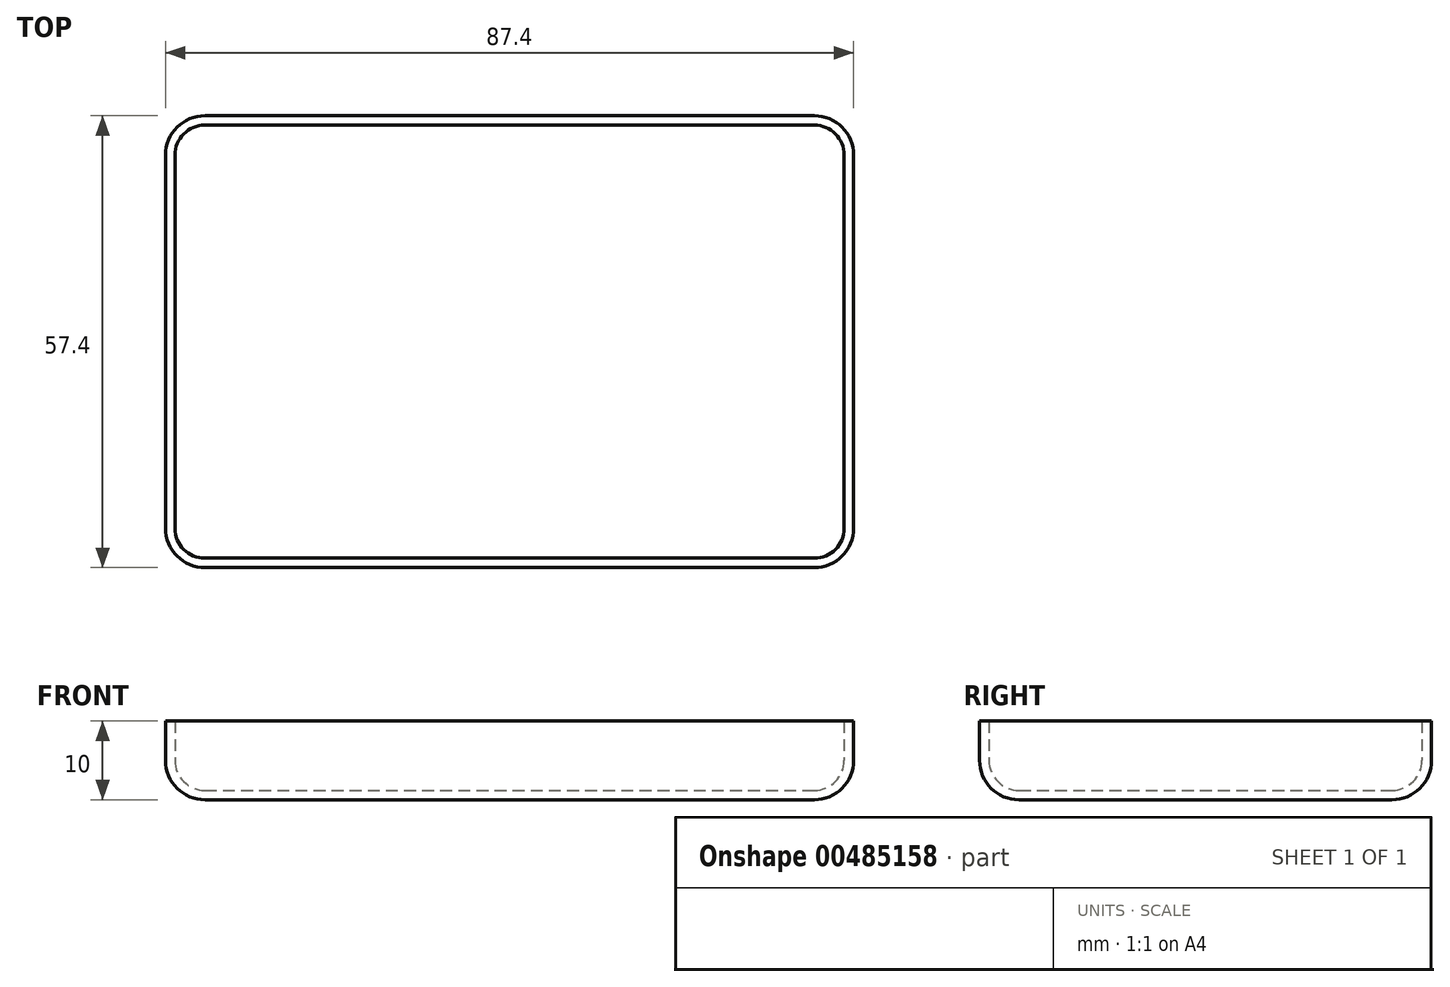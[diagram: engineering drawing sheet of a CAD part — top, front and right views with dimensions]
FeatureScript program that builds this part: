
annotation { "Feature Type Name" : "Feature", "Feature Type Description" : "" }
export const myFeature = defineFeature(function(context is Context, id is Id, definition is map)
    precondition{}
    {
        {
            var Q0;
            Q0=qCreatedBy(makeId("Top.planeOp"),FACE);
            var sketch = newSketch(context, id + "F0", { "sketchPlane" : qUnion([Q0])});
            skLineSegment(sketch, "E0.bottom", {"start": v(42.5, 27.5) * mm, "end": v(-42.5, 27.5) * mm, "construction": true});
            skLineSegment(sketch, "E0.top", {"start": v(42.5, -27.5) * mm, "end": v(-42.5, -27.5) * mm, "construction": true});
            skLineSegment(sketch, "E0.left", {"start": v(42.5, 27.5) * mm, "end": v(42.5, -27.5) * mm, "construction": true});
            skLineSegment(sketch, "E0.right", {"start": v(-42.5, 27.5) * mm, "end": v(-42.5, -27.5) * mm, "construction": true});
            skPoint(sketch, "E0.middle", {"position": v(0, 0) * mm});
            skLineSegment(sketch, "E1.0", {"start": v(43.7, 28.7) * mm, "end": v(-43.7, 28.7) * mm});
            skLineSegment(sketch, "E1.1", {"start": v(43.7, 28.7) * mm, "end": v(43.7, -28.7) * mm});
            skLineSegment(sketch, "E1.2", {"start": v(43.7, -28.7) * mm, "end": v(-43.7, -28.7) * mm});
            skLineSegment(sketch, "E1.3", {"start": v(-43.7, 28.7) * mm, "end": v(-43.7, -28.7) * mm});
            skSolve(sketch);
        }
        {
            var Q0;
            Q0 = qSketchRegion(id + "F0", true);
            extrude(context, id + "F1", {"entities" : qUnion([Q0]), "depth" : 10 * mm});
        }
        {
            var Q0;
            Q0=makeQuery(id+"F1.opExtrude","SWEPT_EDGE",EDGE,{"disambiguationData":[OSD([sQuery(id+"F0.wireOp",EDGE,"E1.1"),sQuery(id+"F0.wireOp",EDGE,"E1.2")])]});
            var Q1;
            Q1=makeQuery(id+"F1.opExtrude","SWEPT_EDGE",EDGE,{"disambiguationData":[OSD([sQuery(id+"F0.wireOp",EDGE,"E1.0"),sQuery(id+"F0.wireOp",EDGE,"E1.1")])]});
            var Q2;
            Q2=makeQuery(id+"F1.opExtrude","SWEPT_EDGE",EDGE,{"disambiguationData":[OSD([sQuery(id+"F0.wireOp",EDGE,"E1.0"),sQuery(id+"F0.wireOp",EDGE,"E1.3")])]});
            var Q3;
            Q3=makeQuery(id+"F1.opExtrude","SWEPT_EDGE",EDGE,{"disambiguationData":[OSD([sQuery(id+"F0.wireOp",EDGE,"E1.2"),sQuery(id+"F0.wireOp",EDGE,"E1.3")])]});
            var Q4;
            Q4=makeQuery(id+"F1.opExtrude","CAP_EDGE",EDGE,{"disambiguationData":[OSD([sQuery(id+"F0.wireOp",EDGE,"E1.3")])],"isStart":true});
            var Q5;
            Q5=makeQuery(id+"F1.opExtrude","CAP_EDGE",EDGE,{"disambiguationData":[OSD([sQuery(id+"F0.wireOp",EDGE,"E1.0")])],"isStart":true});
            var Q6;
            Q6=makeQuery(id+"F1.opExtrude","CAP_EDGE",EDGE,{"disambiguationData":[OSD([sQuery(id+"F0.wireOp",EDGE,"E1.2")])],"isStart":true});
            var Q7;
            Q7=makeQuery(id+"F1.opExtrude","CAP_EDGE",EDGE,{"disambiguationData":[OSD([sQuery(id+"F0.wireOp",EDGE,"E1.1")])],"isStart":true});
            fillet(context, id + "F2", {"entities" : qUnion([Q0, Q1, Q2, Q3, Q4, Q5, Q6, Q7]), "radius" : 5 * mm, "tangentPropagation" : true, "allowEdgeOverflow" : false});
        }
        {
            var Q0;
            Q0=makeQuery(id+"F1.opExtrude","CAP_FACE",FACE,{"disambiguationData":[OSD([sQuery(id+"F0.wireOp",EDGE,"E1.0"),sQuery(id+"F0.wireOp",EDGE,"E1.1"),sQuery(id+"F0.wireOp",EDGE,"E1.2"),sQuery(id+"F0.wireOp",EDGE,"E1.3")])],"isStart":false});
            shell(context, id + "F3", {"entities" : qUnion([Q0]), "thickness" : 1.2 * mm});
        }
    });
